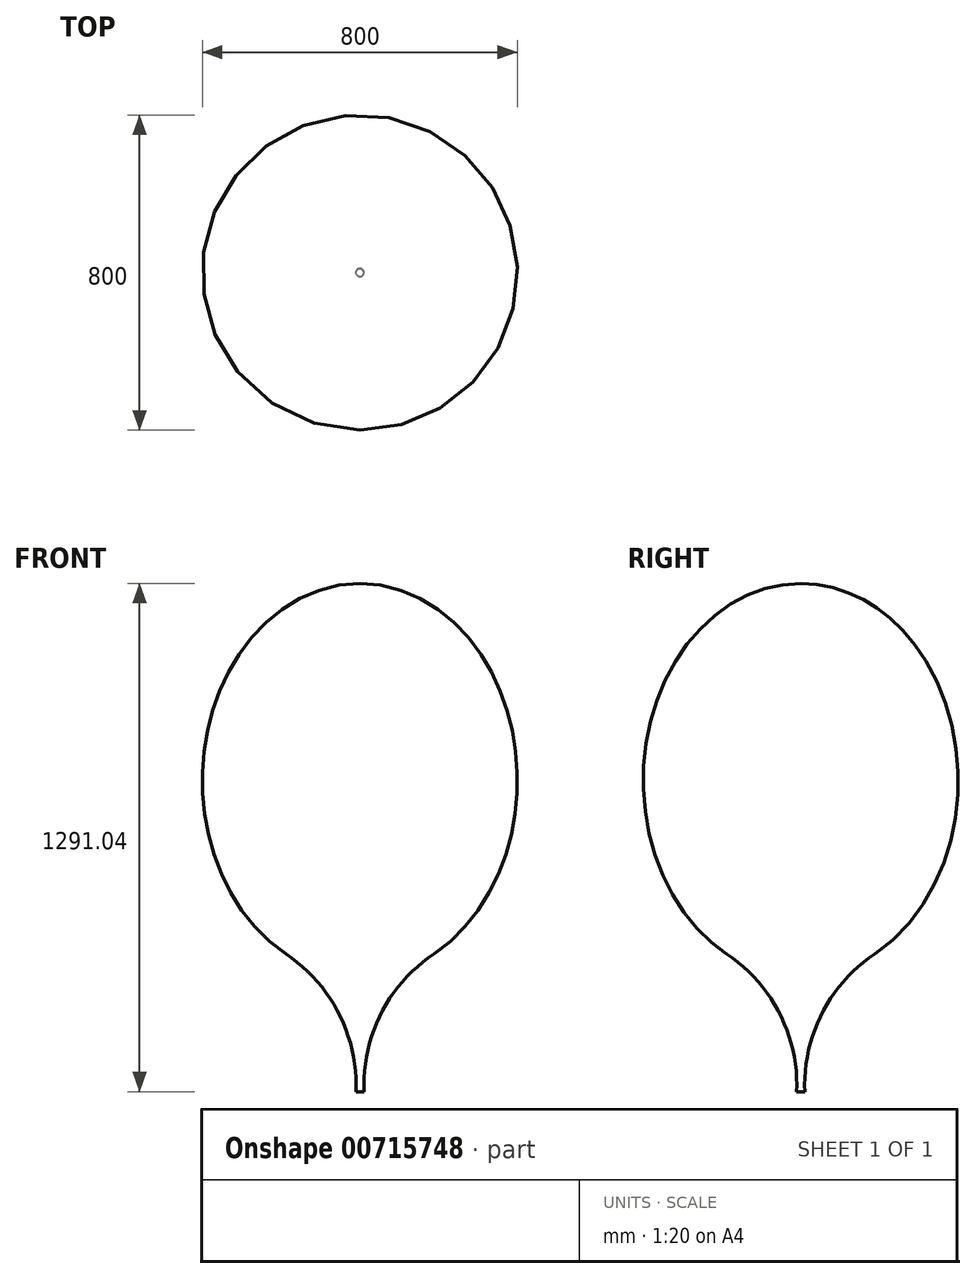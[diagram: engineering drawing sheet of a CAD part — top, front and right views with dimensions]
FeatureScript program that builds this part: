
annotation { "Feature Type Name" : "Feature", "Feature Type Description" : "" }
export const myFeature = defineFeature(function(context is Context, id is Id, definition is map)
    precondition{}
    {
        {
            var Q0;
            Q0=qCreatedBy(makeId("Right.planeOp"),FACE);
            var sketch = newSketch(context, id + "F0", { "sketchPlane" : qUnion([Q0])});
            skEllipticalArc(sketch, "E0", {});
            skLineSegment(sketch, "E1", {"start": v(0, -500) * mm, "end": v(0, 500) * mm});
            skArc(sketch, "E2.filletArc", {"start": v(-10.31, -791.04) * mm, "mid": v(-53.39, -592.83) * mm, "end": v(-188.16, -441.23) * mm});
            skLineSegment(sketch, "E3", {"start": v(0, -500) * mm, "end": v(0, -791.04) * mm});
            skLineSegment(sketch, "E4", {"start": v(-10.31, -791.04) * mm, "end": v(0, -791.04) * mm});
            const initialGuessF0  = {"E0": [0, 0, 0, 1, 0.5, 0.4, 0, 2.6518600089614064]};
            skSetInitialGuess(sketch, initialGuessF0);
            skSolve(sketch);
        }
        {
            var Q0;
            Q0=makeQuery(id+"F0.imprint","IMPRINT",FACE,{"disambiguationData":[TD([[makeQuery(id+"F0.imprint","IMPRINT",EDGE,{"derivedFrom":sQuery(id+"F0.wireOp",EDGE,"E0")}),1.0]])]});
            var Q1;
            Q1=sQuery(id+"F0.wireOp",EDGE,"E1");
            revolve(context, id + "F1", {"surfaceOperationType" : NewSurfaceOperationType.NEW, "entities" : qUnion([Q0]), "axis" : qUnion([Q1]), "revolveType" : RevolveType.FULL});
        }
    });
